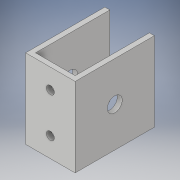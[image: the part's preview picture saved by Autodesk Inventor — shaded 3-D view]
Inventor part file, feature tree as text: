
AUTODESK INVENTOR PART (.ipt)
format: ipt  version: 2019 (Build 230136000, 136)  size: 133,120 bytes
history: native  units: in
note: dims shown in document units (in); Inventor stores cm internally (conversion verified against a paired STEP export)
features: sketch x5, hole x4, extrude x3
ambient origin geometry x8: Origin, YZ Plane, XZ Plane, XY Plane, X Axis, Y Axis, Z Axis, Center Point
bodies: Solid1 (feature_tree)
feature tree (12):
  extrude  "Extrusion1"  Depth=2.0in
  extrude  "Extrusion2"  Depth=0.5in
  extrude  "Extrusion3"  Depth=0.2031in
  hole  "Hole5"  [1 undecoded]
  hole  "Hole7"  [1 undecoded]
  sketch  "Sketch1"  dims[d0=1.0in d1=2.0in]
  sketch  "Sketch2"  dims[d2=0.5in d3=0.5in]
  sketch  "Sketch3"  dims[d4=0.2031in d5=0.2031in]
  sketch  "Sketch6"  dims[d6=0.125in d7=0.0in d8=2.0in]
  hole  "Hole4"  [1 undecoded]
  sketch  "Sketch7"  dims[d9=2.0in d10=0.125in d11=0.0in d12=0.125in d13=0.0in d28=0.375in d29=0.75in d30=0.375in d31=0.25in d32=0.5635in d33=1.0in d34=0.0in d35=0.375in d36=0.75in d37=0.375in d38=0.25in d39=0.5635in d40=1.0in d41=0.0in]
  hole  "Hole6"  [1 undecoded]
note: 4 required parameter values undecoded (feature->parameter linkage not recoverable at this tier; creation-order binding heuristic only, values carry confidence <= 0.55)
